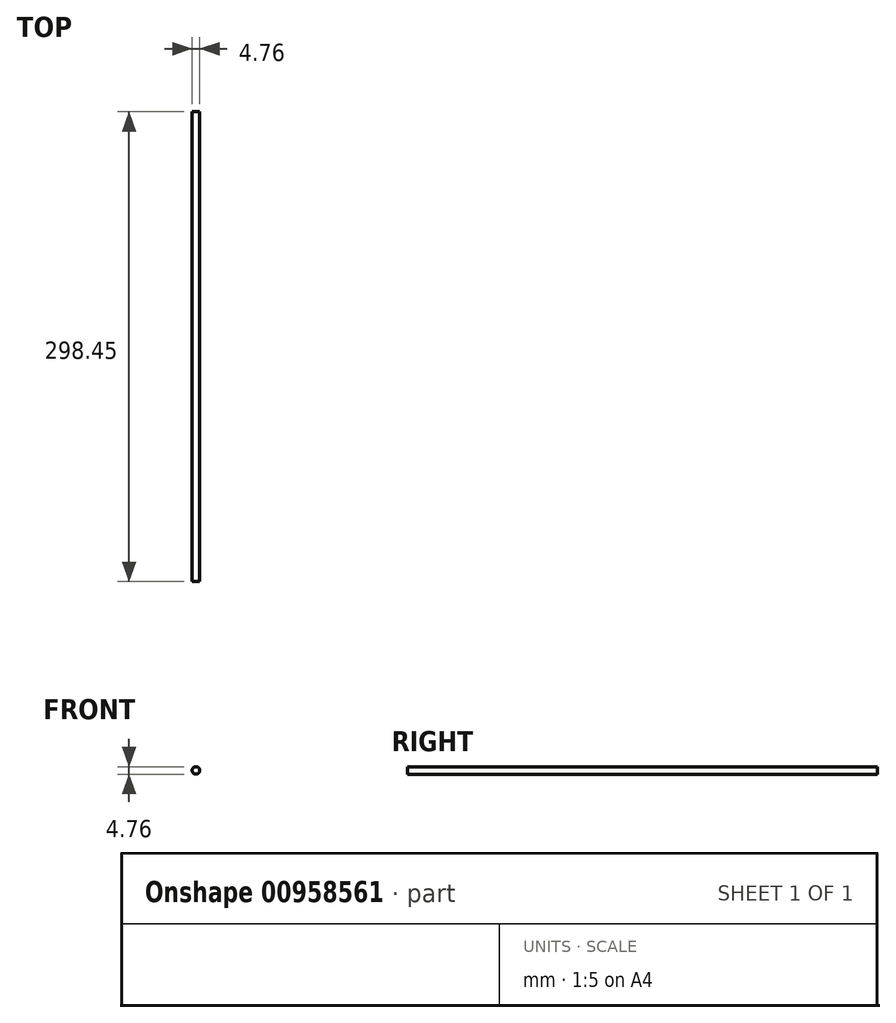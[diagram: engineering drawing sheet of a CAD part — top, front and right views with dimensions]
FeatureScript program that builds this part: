
annotation { "Feature Type Name" : "Feature", "Feature Type Description" : "" }
export const myFeature = defineFeature(function(context is Context, id is Id, definition is map)
    precondition{}
    {
        {
            var Q0;
            Q0=qCreatedBy(makeId("Front.planeOp"),FACE);
            var sketch = newSketch(context, id + "F0", { "sketchPlane" : qUnion([Q0])});
            skCircle(sketch, "E0", {"center": v(0, 0) * mm, "radius": 2.38 * mm});
            skSolve(sketch);
        }
        {
            var Q0;
            Q0=makeQuery(id+"F0.imprint","IMPRINT",FACE,{"disambiguationData":[TD([[makeQuery(id+"F0.imprint","IMPRINT",EDGE,{"derivedFrom":sQuery(id+"F0.wireOp",EDGE,"E0")}),1.0]])]});
            extrude(context, id + "F1", {"entities" : qUnion([Q0]), "depth" : 298.45 * mm, "offsetDistance" : 25.4 * mm});
        }
    });
